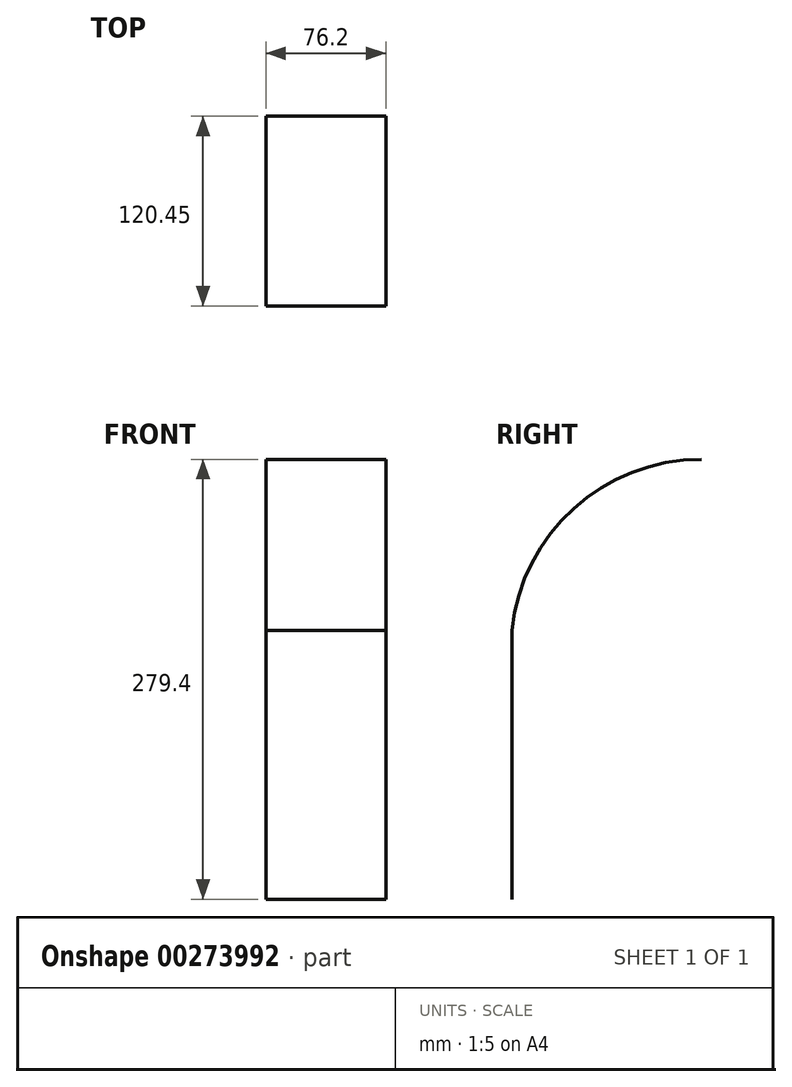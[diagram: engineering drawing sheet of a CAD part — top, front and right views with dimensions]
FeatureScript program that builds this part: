
annotation { "Feature Type Name" : "Feature", "Feature Type Description" : "" }
export const myFeature = defineFeature(function(context is Context, id is Id, definition is map)
    precondition{}
    {
        {
            var Q0;
            Q0=qCreatedBy(makeId("Right.planeOp"),FACE);
            var sketch = newSketch(context, id + "F0", { "sketchPlane" : qUnion([Q0])});
            skArc(sketch, "E0", {"start": v(0, 161.05) * mm, "mid": v(-81.15, 129.83) * mm, "end": v(-120.45, 52.28) * mm});
            skLineSegment(sketch, "E1", {"start": v(-120.45, 52.28) * mm, "end": v(-120.45, -118.35) * mm});
            skSolve(sketch);
        }
        {
            var Q0;
            Q0=sQuery(id+"F0.wireOp",EDGE,"E1");
            var Q1;
            Q1=sQuery(id+"F0.wireOp",EDGE,"E0");
            extrude(context, id + "F1", {"bodyType" : ToolBodyType.SURFACE, "surfaceEntities" : qUnion([Q0, Q1]), "depth" : 76.2 * mm});
        }
    });
